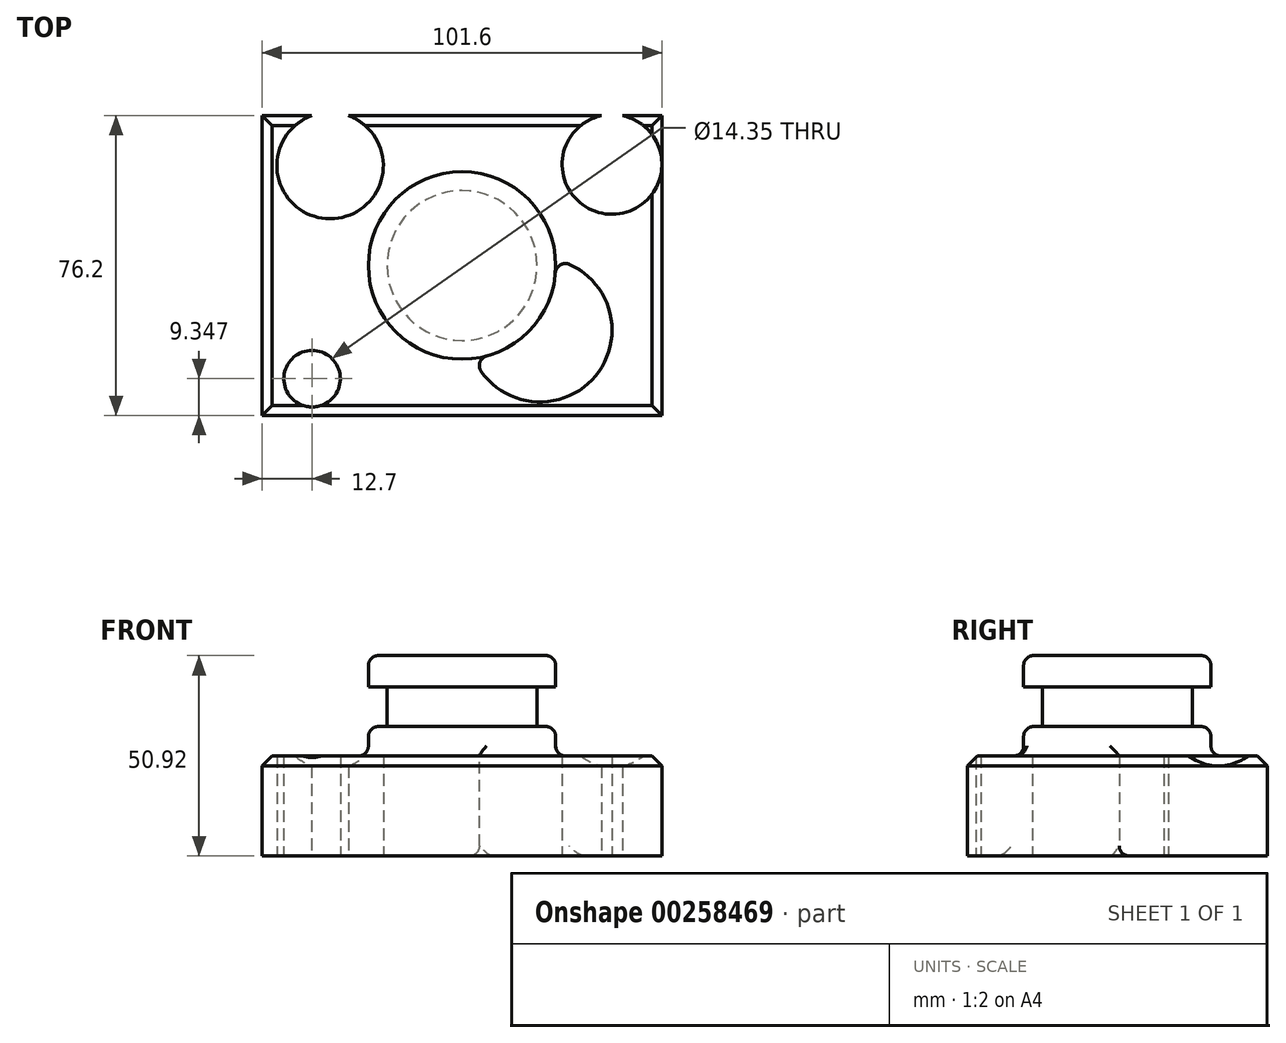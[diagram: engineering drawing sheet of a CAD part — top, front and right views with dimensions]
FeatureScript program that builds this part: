
annotation { "Feature Type Name" : "Feature", "Feature Type Description" : "" }
export const myFeature = defineFeature(function(context is Context, id is Id, definition is map)
    precondition{}
    {
        {
            var Q0;
            Q0=qCreatedBy(makeId("Top.planeOp"),FACE);
            var sketch = newSketch(context, id + "F0", { "sketchPlane" : qUnion([Q0])});
            skLineSegment(sketch, "E0.bottom", {"start": v(-50.8, -38.1) * mm, "end": v(50.8, -38.1) * mm});
            skLineSegment(sketch, "E0.top", {"start": v(-50.8, 38.1) * mm, "end": v(50.8, 38.1) * mm});
            skLineSegment(sketch, "E0.left", {"start": v(-50.8, -38.1) * mm, "end": v(-50.8, 38.1) * mm});
            skLineSegment(sketch, "E0.right", {"start": v(50.8, -38.1) * mm, "end": v(50.8, 38.1) * mm});
            skPoint(sketch, "E0.middle", {"position": v(0, 0) * mm});
            skSolve(sketch);
        }
        {
            var Q0;
            Q0=makeQuery(id+"F0.imprint","IMPRINT",FACE,{"disambiguationData":[TD([[makeQuery(id+"F0.imprint","IMPRINT",EDGE,{"derivedFrom":sQuery(id+"F0.wireOp",EDGE,"E0.bottom")}),1.0]])]});
            extrude(context, id + "F1", {"entities" : qUnion([Q0]), "depth" : 25.4 * mm});
        }
        {
            var Q0;
            Q0=makeQuery(id+"F1.opExtrude","CAP_FACE",FACE,{"disambiguationData":[OSD([sQuery(id+"F0.wireOp",EDGE,"E0.bottom"),sQuery(id+"F0.wireOp",EDGE,"E0.top"),sQuery(id+"F0.wireOp",EDGE,"E0.left"),sQuery(id+"F0.wireOp",EDGE,"E0.right")])],"isStart":true});
            var sketch = newSketch(context, id + "F2", { "sketchPlane" : qUnion([Q0])});
            skCircle(sketch, "E1", {"center": v(19.82, 16.39) * mm, "radius": 18.28 * mm});
            skCircle(sketch, "E2", {"center": v(38.1, -25.7) * mm, "radius": 12.67 * mm});
            skCircle(sketch, "E3", {"center": v(-33.52, -25.4) * mm, "radius": 13.52 * mm});
            skCircle(sketch, "E4", {"center": v(-38.1, 28.75) * mm, "radius": 7.18 * mm});
            skSolve(sketch);
        }
        {
            var Q0;
            Q0 = qSketchRegion(id + "F2", true);
            extrude(context, id + "F3", {"entities" : qUnion([Q0]), "operationType" : NewBodyOperationType.REMOVE, "endBound" : BoundingType.THROUGH_ALL, "oppositeDirection" : true, "depth" : 25.4 * mm, "hasSecondDirection" : true, "secondDirectionOppositeDirection" : false, "secondDirectionDepth" : 25.4 * mm});
        }
        {
            var Q0;
            Q0=qCreatedBy(makeId("Front.planeOp"),FACE);
            var sketch = newSketch(context, id + "F4", { "sketchPlane" : qUnion([Q0])});
            skLineSegment(sketch, "E5.bottom", {"start": v(0, 0) * mm, "end": v(-23.8, 0) * mm});
            skLineSegment(sketch, "E5.top", {"start": v(0, 50.92) * mm, "end": v(-23.8, 50.92) * mm});
            skLineSegment(sketch, "E5.left", {"start": v(0, 0) * mm, "end": v(0, 50.92) * mm});
            skLineSegment(sketch, "E5.right", {"start": v(-23.8, 0) * mm, "end": v(-23.8, 50.92) * mm});
            skSolve(sketch);
        }
        {
            var Q0;
            Q0=makeQuery(id+"F4.imprint","IMPRINT",FACE,{"disambiguationData":[TD([[makeQuery(id+"F4.imprint","IMPRINT",EDGE,{"derivedFrom":sQuery(id+"F4.wireOp",EDGE,"E5.bottom")}),-1.0]])]});
            var Q1;
            Q1=sQuery(id+"F4.wireOp",EDGE,"E5.left");
            revolve(context, id + "F5", {"operationType" : NewBodyOperationType.ADD, "entities" : qUnion([Q0]), "axis" : qUnion([Q1]), "revolveType" : RevolveType.FULL});
        }
        {
            var Q0;
            Q0=qCreatedBy(makeId("Front.planeOp"),FACE);
            var sketch = newSketch(context, id + "F6", { "sketchPlane" : qUnion([Q0])});
            skLineSegment(sketch, "E6.bottom", {"start": v(-19.05, 32.89) * mm, "end": v(-33.09, 32.89) * mm});
            skLineSegment(sketch, "E6.top", {"start": v(-19.05, 42.91) * mm, "end": v(-33.09, 42.91) * mm});
            skLineSegment(sketch, "E6.left", {"start": v(-19.05, 32.89) * mm, "end": v(-19.05, 42.91) * mm});
            skLineSegment(sketch, "E6.right", {"start": v(-33.09, 32.89) * mm, "end": v(-33.09, 42.91) * mm});
            skSolve(sketch);
        }
        {
            var Q0;
            Q0=makeQuery(id+"F6.imprint","IMPRINT",FACE,{"disambiguationData":[TD([[makeQuery(id+"F6.imprint","IMPRINT",EDGE,{"derivedFrom":sQuery(id+"F6.wireOp",EDGE,"E6.bottom")}),-1.0]])]});
            var Q1;
            Q1=makeQuery(id+"F5.opRevolve","SWEPT_FACE",FACE,{"disambiguationData":[OSD([sQuery(id+"F4.wireOp",EDGE,"E5.right")])]});
            revolve(context, id + "F7", {"operationType" : NewBodyOperationType.REMOVE, "entities" : qUnion([Q0]), "axis" : qUnion([Q1]), "revolveType" : RevolveType.FULL, "oppositeDirection" : true});
        }
        {
            var Q0;
            Q0=makeQuery(id+"F5.opRevolve","SWEPT_FACE",FACE,{"disambiguationData":[OSD([sQuery(id+"F4.wireOp",EDGE,"E5.top")])]});
            var Q1;
            Q1=makeQuery(id+"F7.boolean.opBoolean","SPLIT",FACE,{"disambiguationData":[TD([makeQuery(id+"F3.boolean.opBoolean","COPY",FACE,{"derivedFrom":makeQuery(id+"F3.opExtrude","SWEPT_FACE",FACE,{"disambiguationData":[OSD([sQuery(id+"F2.wireOp",EDGE,"E1")])]})})])],"derivedFrom":makeQuery(id+"F5.opRevolve","SWEPT_FACE",FACE,{"disambiguationData":[OSD([sQuery(id+"F4.wireOp",EDGE,"E5.right")])]})});
            fillet(context, id + "F8", {"entities" : qUnion([Q0, Q1]), "radius" : 2.54 * mm, "tangentPropagation" : true, "allowEdgeOverflow" : false});
        }
        {
            var Q0;
            Q0=makeQuery(id+"F1.opExtrude","CAP_EDGE",EDGE,{"disambiguationData":[OSD([sQuery(id+"F0.wireOp",EDGE,"E0.bottom")])],"isStart":false});
            var Q1;
            Q1=makeQuery(id+"F1.opExtrude","CAP_EDGE",EDGE,{"disambiguationData":[OSD([sQuery(id+"F0.wireOp",EDGE,"E0.left")])],"isStart":false});
            var Q2;
            Q2=makeQuery(id+"F1.opExtrude","CAP_EDGE",EDGE,{"disambiguationData":[OSD([sQuery(id+"F0.wireOp",EDGE,"E0.right")])],"isStart":false});
            var Q3;
            {var subQ0=sQuery(id+"F0.wireOp",EDGE,"E0.top");Q3=makeQuery(id+"F3.boolean.opBoolean","SPLIT",EDGE,{"disambiguationData":[TD([makeQuery(id+"F1.opExtrude","CAP_FACE",FACE,{"disambiguationData":[OSD([sQuery(id+"F0.wireOp",EDGE,"E0.bottom"),subQ0,sQuery(id+"F0.wireOp",EDGE,"E0.left"),sQuery(id+"F0.wireOp",EDGE,"E0.right")])],"isStart":false}),makeQuery(id+"F1.opExtrude","SWEPT_FACE",FACE,{"disambiguationData":[OSD([subQ0])]}),makeQuery(id+"F3.opExtrude","SWEPT_FACE",FACE,{"disambiguationData":[OSD([sQuery(id+"F2.wireOp",EDGE,"E2")])]}),makeQuery(id+"F3.opExtrude","SWEPT_FACE",FACE,{"disambiguationData":[OSD([sQuery(id+"F2.wireOp",EDGE,"E3")])]})])],"derivedFrom":makeQuery(id+"F1.opExtrude","CAP_EDGE",EDGE,{"disambiguationData":[OSD([subQ0])],"isStart":false})});}
            var Q4;
            {var subQ0=sQuery(id+"F0.wireOp",EDGE,"E0.right");var subQ1=sQuery(id+"F0.wireOp",EDGE,"E0.top");Q4=makeQuery(id+"F3.boolean.opBoolean","SPLIT",EDGE,{"disambiguationData":[TD([makeQuery(id+"F1.opExtrude","CAP_FACE",FACE,{"disambiguationData":[OSD([sQuery(id+"F0.wireOp",EDGE,"E0.bottom"),subQ1,sQuery(id+"F0.wireOp",EDGE,"E0.left"),subQ0])],"isStart":false}),makeQuery(id+"F1.opExtrude","SWEPT_FACE",FACE,{"disambiguationData":[OSD([subQ1])]}),makeQuery(id+"F1.opExtrude","SWEPT_FACE",FACE,{"disambiguationData":[OSD([subQ0])]}),makeQuery(id+"F3.opExtrude","SWEPT_FACE",FACE,{"disambiguationData":[OSD([sQuery(id+"F2.wireOp",EDGE,"E2")])]})])],"derivedFrom":makeQuery(id+"F1.opExtrude","CAP_EDGE",EDGE,{"disambiguationData":[OSD([subQ1])],"isStart":false})});}
            var Q5;
            {var subQ0=sQuery(id+"F0.wireOp",EDGE,"E0.left");var subQ1=sQuery(id+"F0.wireOp",EDGE,"E0.top");Q5=makeQuery(id+"F3.boolean.opBoolean","SPLIT",EDGE,{"disambiguationData":[TD([makeQuery(id+"F1.opExtrude","CAP_FACE",FACE,{"disambiguationData":[OSD([sQuery(id+"F0.wireOp",EDGE,"E0.bottom"),subQ1,subQ0,sQuery(id+"F0.wireOp",EDGE,"E0.right")])],"isStart":false}),makeQuery(id+"F1.opExtrude","SWEPT_FACE",FACE,{"disambiguationData":[OSD([subQ1])]}),makeQuery(id+"F1.opExtrude","SWEPT_FACE",FACE,{"disambiguationData":[OSD([subQ0])]}),makeQuery(id+"F3.opExtrude","SWEPT_FACE",FACE,{"disambiguationData":[OSD([sQuery(id+"F2.wireOp",EDGE,"E3")])]})])],"derivedFrom":makeQuery(id+"F1.opExtrude","CAP_EDGE",EDGE,{"disambiguationData":[OSD([subQ1])],"isStart":false})});}
            chamfer(context, id + "F9", {"entities" : qUnion([Q0, Q1, Q2, Q3, Q4, Q5]), "width" : 2.54 * mm, "tangentPropagation" : true});
        }
    });
